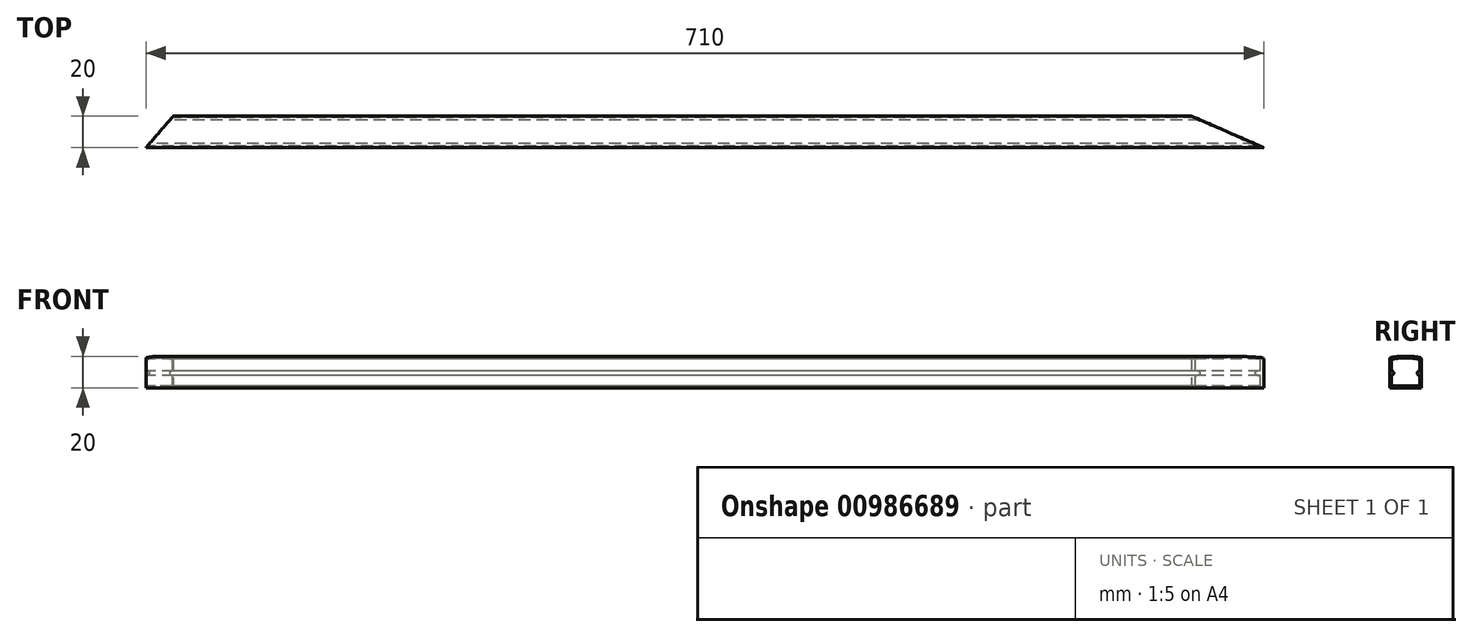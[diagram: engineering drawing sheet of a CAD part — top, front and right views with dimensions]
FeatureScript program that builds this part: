
annotation { "Feature Type Name" : "Feature", "Feature Type Description" : "" }
export const myFeature = defineFeature(function(context is Context, id is Id, definition is map)
    precondition{}
    {
        {
            var Q0;
            Q0=qCreatedBy(makeId("Right.planeOp"),FACE);
            var sketch = newSketch(context, id + "F0", { "sketchPlane" : qUnion([Q0])});
            skLineSegment(sketch, "E0.bottom", {"start": v(-10, -10) * mm, "end": v(10, -10) * mm});
            skLineSegment(sketch, "E0.top", {"start": v(-10, 10) * mm, "end": v(10, 10) * mm});
            skLineSegment(sketch, "E0.left", {"start": v(-10, -10) * mm, "end": v(-10, 10) * mm});
            skLineSegment(sketch, "E0.right", {"start": v(10, -10) * mm, "end": v(10, 10) * mm});
            skPoint(sketch, "E0.middle", {"position": v(0, 0) * mm});
            skSolve(sketch);
        }
        {
            var Q0;
            Q0=qCreatedBy(makeId("Right.planeOp"),FACE);
            var sketch = newSketch(context, id + "F1", { "sketchPlane" : qUnion([Q0])});
            skLineSegment(sketch, "E1.0", {"start": v(0, -10) * mm, "end": v(10, -10) * mm});
            skLineSegment(sketch, "E1.3", {"start": v(10, -10) * mm, "end": v(10, -0.2) * mm});
            skPoint(sketch, "E1.4", {"position": v(0, 0) * mm});
            skLineSegment(sketch, "E2.0", {"start": v(9, -9) * mm, "end": v(9, -2.2) * mm});
            skLineSegment(sketch, "E2.1", {"start": v(0, -9) * mm, "end": v(9, -9) * mm});
            skLineSegment(sketch, "E3", {"start": v(10, -0.2) * mm, "end": v(9, -0.2) * mm});
            skArc(sketch, "E4", {"start": v(9, -0.2) * mm, "mid": v(8.5, -0.7) * mm, "end": v(9, -1.2) * mm});
            skArc(sketch, "E5", {"start": v(9, -2.2) * mm, "mid": v(9.5, -1.7) * mm, "end": v(9, -1.2) * mm});
            skLineSegment(sketch, "E6", {"start": v(0, -9) * mm, "end": v(0, -10) * mm});
            skPoint(sketch, "E1.1.end.orphan", {"position": v(10, 10) * mm});
            skPoint(sketch, "E1.1.start.orphan", {"position": v(-10, 10) * mm});
            skPoint(sketch, "E1.2.end.orphan", {"position": v(-10, 10) * mm});
            skPoint(sketch, "E1.2.start.orphan", {"position": v(-10, -10) * mm});
            skPoint(sketch, "E7.orphan", {"position": v(-9, -9) * mm});
            skSolve(sketch);
        }
        {
            var Q0;
            Q0=qSketchRegion(id+"F1",true);
            extrude(context, id + "F2", {"entities" : qUnion([Q0]), "depth" : 1000 * mm, "offsetDistance" : 25 * mm});
        }
        {
            var Q0;
            Q0=qCreatedBy(makeId("Right.planeOp"),FACE);
            var sketch = newSketch(context, id + "F3", { "sketchPlane" : qUnion([Q0])});
            skPoint(sketch, "E8.2", {"position": v(0, 0) * mm});
            skLineSegment(sketch, "E8.5", {"start": v(10, -0.2) * mm, "end": v(9, -0.2) * mm});
            skArc(sketch, "E8.6", {"start": v(9, -0.2) * mm, "mid": v(8.5, -0.7) * mm, "end": v(9, -1.2) * mm});
            skArc(sketch, "E8.7", {"start": v(9, -2.2) * mm, "mid": v(9.5, -1.7) * mm, "end": v(9, -1.2) * mm});
            skPoint(sketch, "E8.9", {"position": v(10, 10) * mm});
            skPoint(sketch, "E8.10", {"position": v(10, 10) * mm});
            skPoint(sketch, "E8.11", {"position": v(-10, 10) * mm});
            skPoint(sketch, "E8.12", {"position": v(-10, 10) * mm});
            skPoint(sketch, "E8.13", {"position": v(-10, -10) * mm});
            skPoint(sketch, "E8.14", {"position": v(-9, -9) * mm});
            skPoint(sketch, "E8.15", {"position": v(-10, -10) * mm});
            skPoint(sketch, "E8.1.end.orphan", {"position": v(10, -0.2) * mm});
            skPoint(sketch, "E8.1.start.orphan", {"position": v(10, -10) * mm});
            skPoint(sketch, "E8.3.end.orphan", {"position": v(9, -2.2) * mm});
            skPoint(sketch, "E8.3.start.orphan", {"position": v(9, -9) * mm});
            skPoint(sketch, "E8.4.end.orphan", {"position": v(9, -9) * mm});
            skPoint(sketch, "E8.4.start.orphan", {"position": v(0, -9) * mm});
            skPoint(sketch, "E8.0.end.orphan", {"position": v(10, -10) * mm});
            skPoint(sketch, "E8.0.start.orphan", {"position": v(0, -10) * mm});
            skPoint(sketch, "E8.8.end.orphan", {"position": v(0, -10) * mm});
            skPoint(sketch, "E8.8.start.orphan", {"position": v(0, -9) * mm});
            skLineSegment(sketch, "E9", {"start": v(10, -0.2) * mm, "end": v(10, 8.17) * mm});
            skArc(sketch, "E10", {"start": v(9.18, 9.15) * mm, "mid": v(4.61, 9.79) * mm, "end": v(0, 10) * mm});
            skLineSegment(sketch, "E11", {"start": v(0, 10) * mm, "end": v(-15.57, 10) * mm, "construction": true});
            skPoint(sketch, "E12.visualSharp", {"position": v(10, 8.99) * mm});
            skArc(sketch, "E12.filletArc", {"start": v(10, 8.17) * mm, "mid": v(9.77, 8.8) * mm, "end": v(9.18, 9.15) * mm});
            skArc(sketch, "E13.0", {"start": v(9, 8.17) * mm, "mid": v(4.52, 8.8) * mm, "end": v(0, 9) * mm});
            skLineSegment(sketch, "E13.1", {"start": v(9, 0.8) * mm, "end": v(9, 8.17) * mm});
            skArc(sketch, "E13.2", {"start": v(9, 0.8) * mm, "mid": v(7.5, -0.7) * mm, "end": v(9, -2.2) * mm});
            skLineSegment(sketch, "E14", {"start": v(0, 10) * mm, "end": v(0, 9) * mm});
            skSolve(sketch);
        }
        {
            var Q0;
            Q0=qSketchRegion(id+"F3",true);
            extrude(context, id + "F4", {"entities" : qUnion([Q0]), "depth" : 1000 * mm, "offsetDistance" : 25 * mm});
        }
        {
            var Q0;
            Q0=makeQuery(id+"F2.opExtrude","SWEPT_BODY",BODY,{"disambiguationData":[OSD([sQuery(id+"F1.wireOp",EDGE,"E1.0"),sQuery(id+"F1.wireOp",EDGE,"E1.3"),sQuery(id+"F1.wireOp",EDGE,"E2.0"),sQuery(id+"F1.wireOp",EDGE,"E2.1"),sQuery(id+"F1.wireOp",EDGE,"E3"),sQuery(id+"F1.wireOp",EDGE,"E4"),sQuery(id+"F1.wireOp",EDGE,"E5"),sQuery(id+"F1.wireOp",EDGE,"E6")])]});
            var Q1;
            Q1=qCreatedBy(makeId("Front.planeOp"),FACE);
            mirror(context, id + "F5", {"operationType" : NewBodyOperationType.ADD, "entities" : qUnion([Q0]), "mirrorPlane" : qUnion([Q1])});
        }
        {
            var Q0;
            Q0=makeQuery(id+"F4.opExtrude","SWEPT_BODY",BODY,{"disambiguationData":[OSD([sQuery(id+"F3.wireOp",EDGE,"E8.5"),sQuery(id+"F3.wireOp",EDGE,"E8.6"),sQuery(id+"F3.wireOp",EDGE,"E8.7"),sQuery(id+"F3.wireOp",EDGE,"E9"),sQuery(id+"F3.wireOp",EDGE,"E10"),sQuery(id+"F3.wireOp",EDGE,"E12.filletArc"),sQuery(id+"F3.wireOp",EDGE,"E13.0"),sQuery(id+"F3.wireOp",EDGE,"E13.1"),sQuery(id+"F3.wireOp",EDGE,"E13.2"),sQuery(id+"F3.wireOp",EDGE,"E14")])]});
            var Q1;
            Q1=qCreatedBy(makeId("Front.planeOp"),FACE);
            mirror(context, id + "F6", {"operationType" : NewBodyOperationType.ADD, "entities" : qUnion([Q0]), "mirrorPlane" : qUnion([Q1])});
        }
        {
            var Q0;
            Q0=qCreatedBy(makeId("Top.planeOp"),FACE);
            var sketch = newSketch(context, id + "F7", { "sketchPlane" : qUnion([Q0])});
            skLineSegment(sketch, "E15", {"start": v(0, 0) * mm, "end": v(0, -10) * mm});
            skLineSegment(sketch, "E16", {"start": v(0, -10) * mm, "end": v(17.39, 10) * mm});
            skLineSegment(sketch, "E17", {"start": v(17.39, 10) * mm, "end": v(0, 10) * mm});
            skLineSegment(sketch, "E18", {"start": v(0, 10) * mm, "end": v(0, 0) * mm});
            skLineSegment(sketch, "E19", {"start": v(710, -10) * mm, "end": v(664, 10) * mm});
            skLineSegment(sketch, "E20", {"start": v(664, 10) * mm, "end": v(709.91, 10) * mm});
            skLineSegment(sketch, "E21.bottom", {"start": v(710, -10) * mm, "end": v(1016.96, -10) * mm});
            skLineSegment(sketch, "E21.top", {"start": v(709.91, 10) * mm, "end": v(1016.96, 10) * mm});
            skLineSegment(sketch, "E21.right", {"start": v(1016.96, -10) * mm, "end": v(1016.96, 10) * mm});
            skLineSegment(sketch, "E22", {"start": v(710, -10) * mm, "end": v(709.91, 10) * mm, "construction": true});
            skSolve(sketch);
        }
        {
            var Q0;
            Q0 = qSketchRegion(id + "F7", true);
            extrude(context, id + "F8", {"entities" : qUnion([Q0]), "operationType" : NewBodyOperationType.REMOVE, "endBound" : BoundingType.THROUGH_ALL, "depth" : 25 * mm, "offsetDistance" : 25 * mm, "hasSecondDirection" : true, "secondDirectionBound" : SecondDirectionBoundingType.THROUGH_ALL, "secondDirectionOppositeDirection" : true, "secondDirectionDepth" : 25 * mm});
        }
    });
